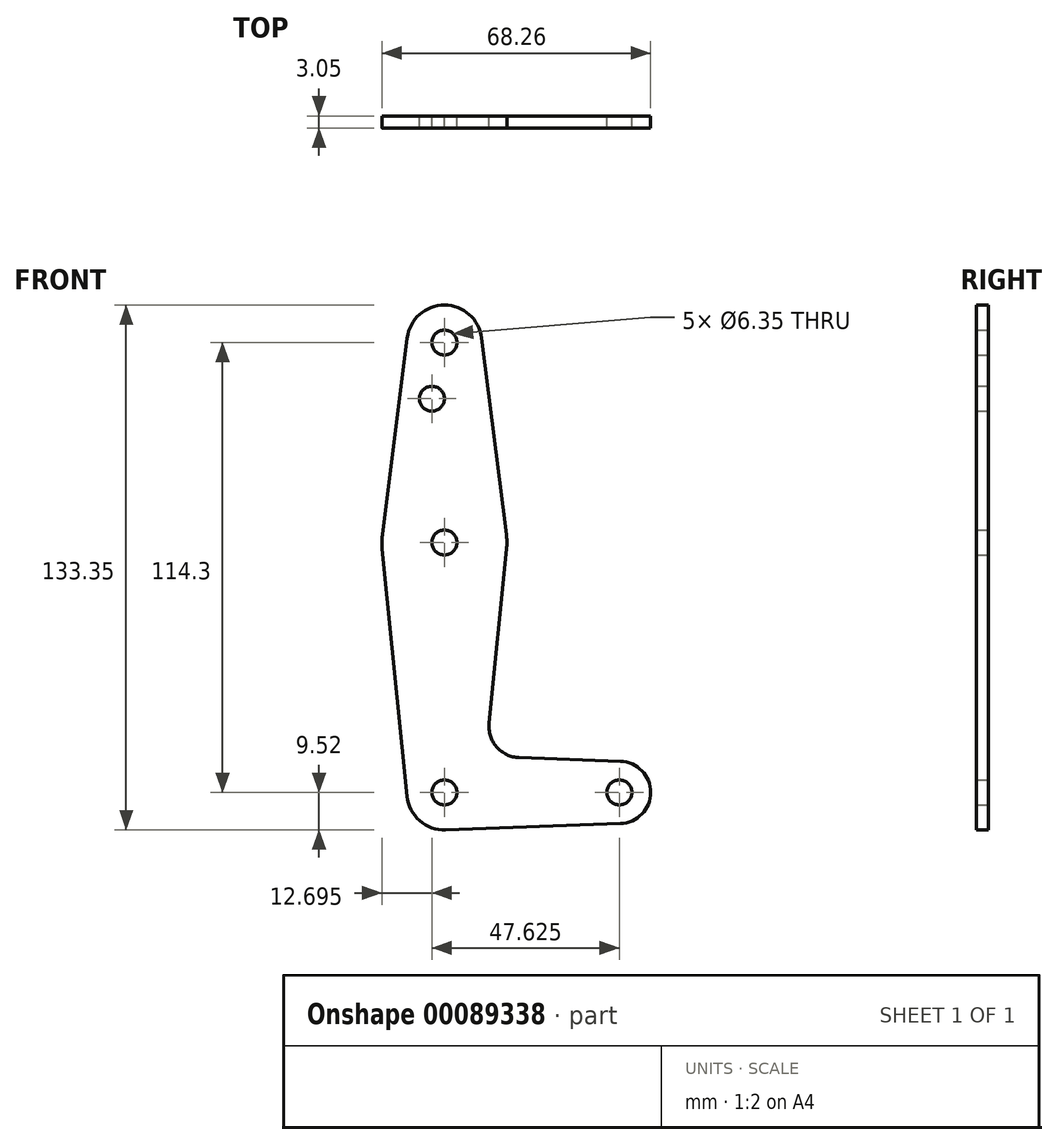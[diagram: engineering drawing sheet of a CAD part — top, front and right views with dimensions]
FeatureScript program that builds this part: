
annotation { "Feature Type Name" : "Feature", "Feature Type Description" : "" }
export const myFeature = defineFeature(function(context is Context, id is Id, definition is map)
    precondition{}
    {
        {
            var Q0;
            Q0=qCreatedBy(makeId("Front.planeOp"),FACE);
            var sketch = newSketch(context, id + "F0", { "sketchPlane" : qUnion([Q0])});
            skCircle(sketch, "E0", {"center": v(0, 114.3) * mm, "radius": 9.53 * mm});
            skCircle(sketch, "E1", {"center": v(0, 63.5) * mm, "radius": 15.88 * mm});
            skCircle(sketch, "E2", {"center": v(0, 0) * mm, "radius": 9.53 * mm});
            skCircle(sketch, "E3", {"center": v(44.45, 0) * mm, "radius": 7.94 * mm});
            skLineSegment(sketch, "E4", {"start": v(9.45, 115.5) * mm, "end": v(15.75, 65.48) * mm});
            skLineSegment(sketch, "E5", {"start": v(-9.45, 115.5) * mm, "end": v(-15.75, 65.48) * mm});
            skLineSegment(sketch, "E6", {"start": v(-15.8, 61.91) * mm, "end": v(-9.48, -0.95) * mm});
            skLineSegment(sketch, "E7", {"start": v(15.8, 61.91) * mm, "end": v(11.34, 17.6) * mm});
            skLineSegment(sketch, "E8", {"start": v(18.97, 8.85) * mm, "end": v(44.73, 7.93) * mm});
            skLineSegment(sketch, "E9", {"start": v(44.73, -7.93) * mm, "end": v(0.34, -9.52) * mm});
            skCircle(sketch, "E10", {"center": v(-3.17, 100.03) * mm, "radius": 3.18 * mm});
            skCircle(sketch, "E11", {"center": v(0, 114.3) * mm, "radius": 3.18 * mm});
            skCircle(sketch, "E12", {"center": v(0, 63.5) * mm, "radius": 3.18 * mm});
            skCircle(sketch, "E13", {"center": v(0, 0) * mm, "radius": 3.18 * mm});
            skCircle(sketch, "E14", {"center": v(44.45, 0) * mm, "radius": 3.18 * mm});
            skArc(sketch, "E15", {"start": v(11.34, 17.6) * mm, "mid": v(13.26, 11.57) * mm, "end": v(18.97, 8.85) * mm});
            skPoint(sketch, "E15.endSnap0", {"position": v(22.54, 8.73) * mm});
            skPoint(sketch, "E16.orphan", {"position": v(9.57, 0) * mm});
            skPoint(sketch, "E17.orphan", {"position": v(22.54, 9.56) * mm});
            skPoint(sketch, "E18.orphan", {"position": v(0.34, 9.52) * mm});
            skSolve(sketch);
        }
        {
            var Q0;
            Q0 = qSketchRegion(id + "F0", true);
            extrude(context, id + "F1", {"entities" : qUnion([Q0]), "depth" : 3.05 * mm});
        }
    });
